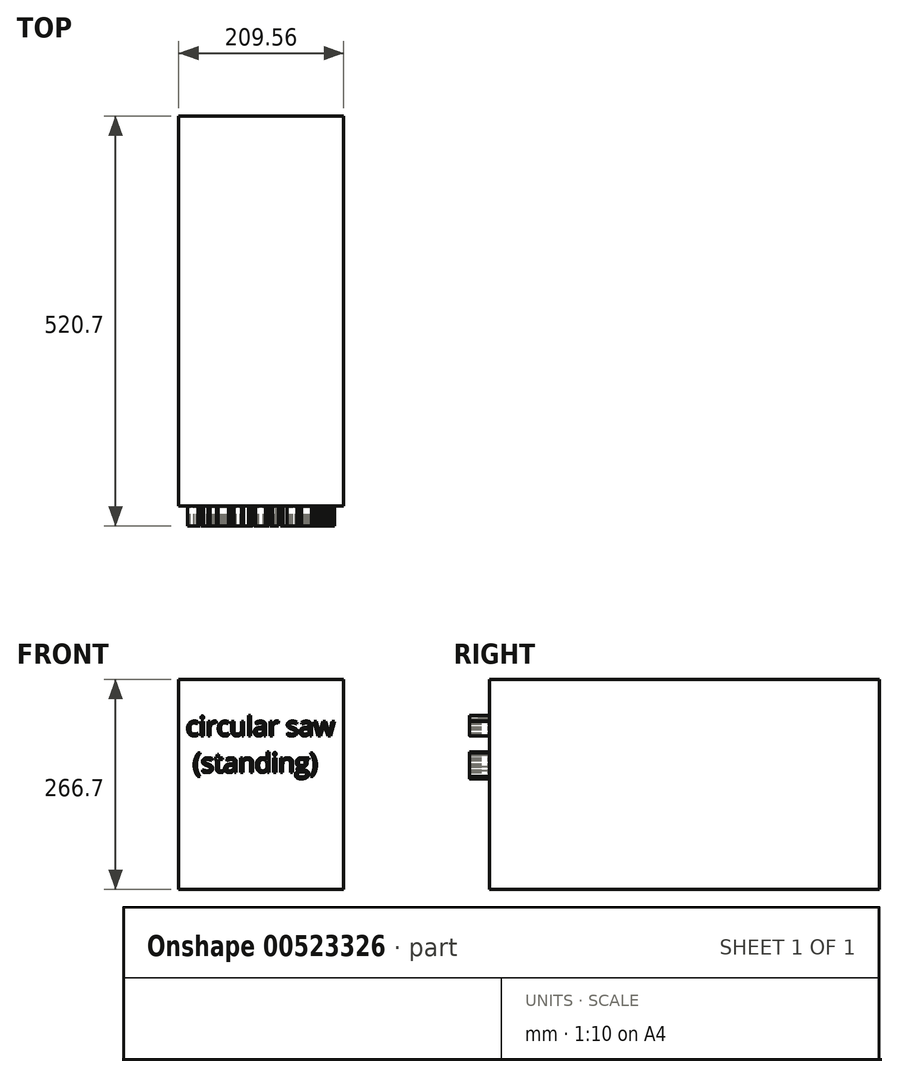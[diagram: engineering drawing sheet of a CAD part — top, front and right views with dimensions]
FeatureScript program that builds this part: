
annotation { "Feature Type Name" : "Feature", "Feature Type Description" : "" }
export const myFeature = defineFeature(function(context is Context, id is Id, definition is map)
    precondition{}
    {
        {
            var Q0;
            Q0=qCreatedBy(makeId("Front.planeOp"),FACE);
            var sketch = newSketch(context, id + "F0", { "sketchPlane" : qUnion([Q0])});
            skLineSegment(sketch, "E0.bottom", {"start": v(104.77, 133.35) * mm, "end": v(-104.78, 133.35) * mm});
            skLineSegment(sketch, "E0.top", {"start": v(104.78, -133.35) * mm, "end": v(-104.77, -133.35) * mm});
            skLineSegment(sketch, "E0.left", {"start": v(104.77, 133.35) * mm, "end": v(104.78, -133.35) * mm});
            skLineSegment(sketch, "E0.right", {"start": v(-104.78, 133.35) * mm, "end": v(-104.77, -133.35) * mm});
            skPoint(sketch, "E0.middle", {"position": v(0, 0) * mm});
            skSolve(sketch);
        }
        {
            var Q0;
            Q0=makeQuery(id+"F0.imprint","IMPRINT",FACE,{"disambiguationData":[TD([[makeQuery(id+"F0.imprint","IMPRINT",EDGE,{"derivedFrom":sQuery(id+"F0.wireOp",EDGE,"E0.bottom")}),1.0]])]});
            extrude(context, id + "F1", {"entities" : qUnion([Q0]), "depth" : 495.3 * mm, "offsetDistance" : 25.4 * mm});
        }
        {
            var Q0;
            Q0=makeQuery(id+"F1.opExtrude","CAP_FACE",FACE,{"disambiguationData":[OSD([sQuery(id+"F0.wireOp",EDGE,"E0.bottom"),sQuery(id+"F0.wireOp",EDGE,"E0.top"),sQuery(id+"F0.wireOp",EDGE,"E0.left"),sQuery(id+"F0.wireOp",EDGE,"E0.right")])],"isStart":false});
            var sketch = newSketch(context, id + "F2", { "sketchPlane" : qUnion([Q0])});
            skText(sketch, "E1", { "text": "circular saw\n (standing)", "fontName": "OpenSans-Regular.ttf"});
            const initialGuessF2  = {"E1": [-0.09534, 0.06189, 1, 0, 0.02463]};
            skSetInitialGuess(sketch, initialGuessF2);
            skSolve(sketch);
        }
        {
            var Q0;
            Q0 = qSketchRegion(id + "F2", true);
            extrude(context, id + "F3", {"entities" : qUnion([Q0]), "operationType" : NewBodyOperationType.ADD, "depth" : 25.4 * mm, "offsetDistance" : 25.4 * mm});
        }
    });
